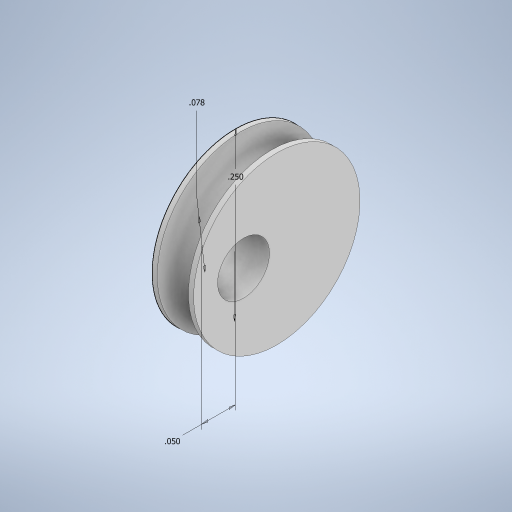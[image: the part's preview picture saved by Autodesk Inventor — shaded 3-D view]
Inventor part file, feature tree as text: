
AUTODESK INVENTOR PART (.ipt)
format: ipt  version: 2023 (Build 270158000, 158)  size: 272,896 bytes
history: native  units: in
note: dims shown in document units (in); Inventor stores cm internally (conversion verified against a paired STEP export)
features: sketch x2, extrude x1, revolve x1
ambient origin geometry x8: Origin, YZ Plane, XZ Plane, XY Plane, X Axis, Y Axis, Z Axis, Center Point
bodies: Solid1 (feature_tree)
feature tree (4):
  extrude  "Extrusion1"  Depth=0.0781in
  revolve  "Revolution1"  [1 undecoded]
  sketch  "Sketch1"  dims[d0=0.25in d1=0.0781in]
  sketch  "Sketch2"  dims[d2=0.05in d3=0.0625in d4=0.0in d5=0.0469in d6=90.0deg]
note: 1 required parameter value undecoded (feature->parameter linkage not recoverable at this tier; creation-order binding heuristic only, values carry confidence <= 0.55)
